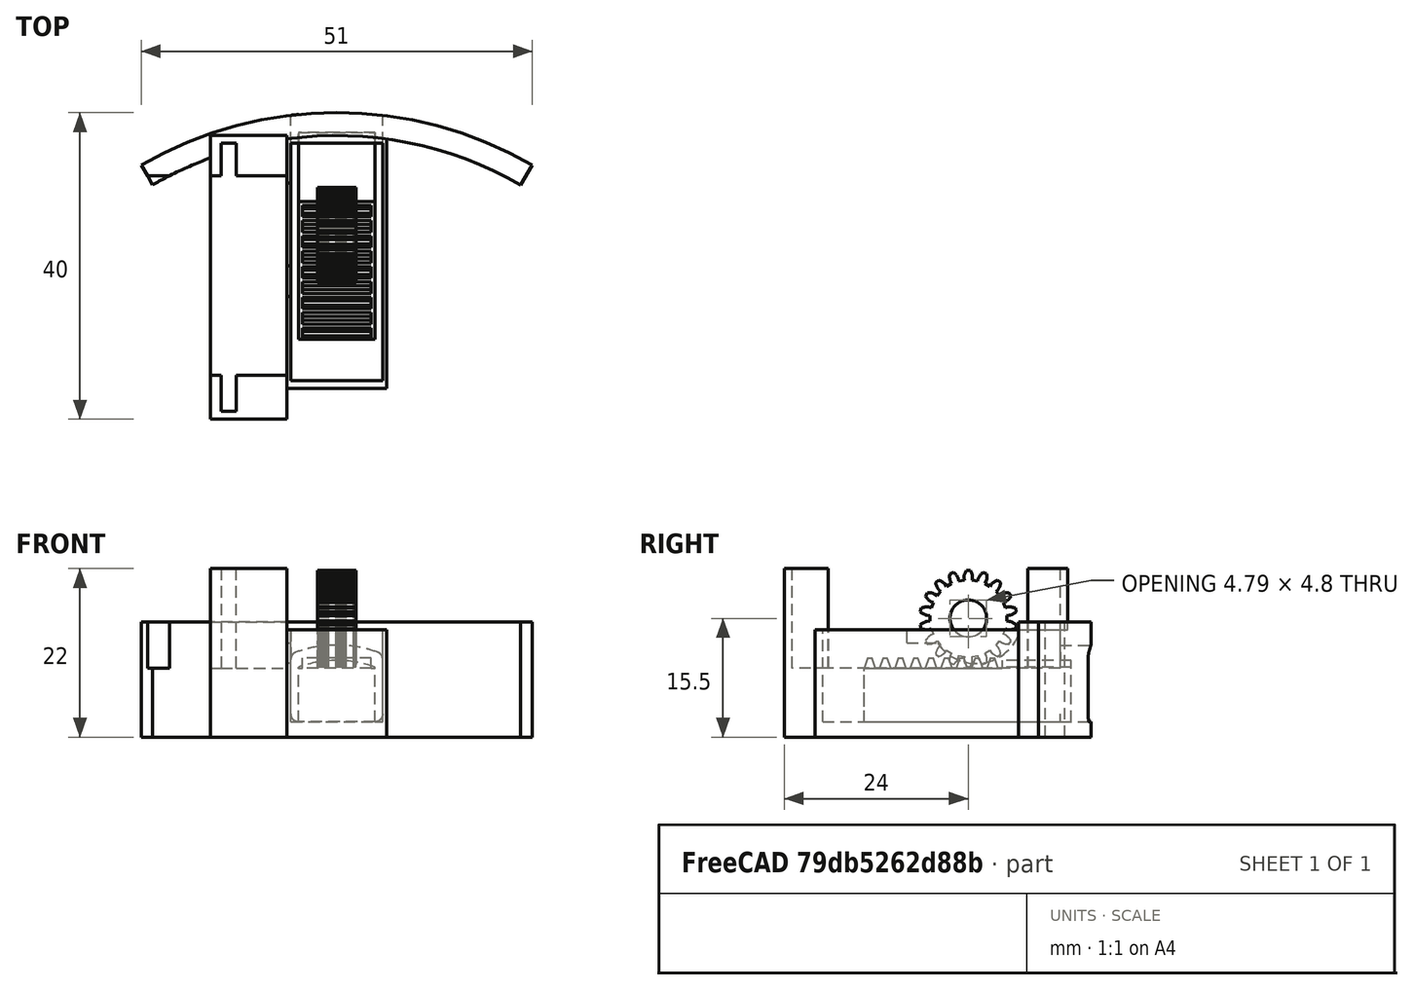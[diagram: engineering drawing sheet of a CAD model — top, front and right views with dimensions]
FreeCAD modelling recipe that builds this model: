
FCSTD DOCUMENT  (FreeCAD 0.16R4924 (Git))
Label: interior_servo_bay_v4p13
License: All rights reserved
LicenseURL: http://en.wikipedia.org/wiki/All_rights_reserved
objects: Part::Feature×11, Part::Box×9, Part::Cut×6, Part::MultiFuse×6, Part::Cylinder×4, Part::Extrusion×3, Part::Thickness×1, Mesh::Feature×1, Part::Fuse×1, Part::FeaturePython×1, Part::Prism×1, Part::MultiCommon×1
note: 44 computed .brp shape members not serialized (recipe doc carries the construction recipe); baked Part::Feature solids carry a one-line shape summary decoded from their .brp

FEATURE [Part::Cylinder] Cylinder  label="bottle_wall"
  Angle = 60
  Height = 15
  Placement = pos=(8.5,-7,0) rot=(0,0,1;1.0472rad)
  Radius = 51
FEATURE [Part::Cylinder] Cylinder001  label="bottle_wall001"
  Angle = 60
  Height = 15
  Placement = pos=(8.5,-7,0) rot=(0,0,1;1.0472rad)
  Radius = 48
FEATURE [Part::Cut] Cut  label="bottle_wall_composite"
  Base = -> Cylinder
  Placement = pos=(0,-2,0) rot=(0,0,1;0rad)
  Tool = -> Cylinder001
FEATURE [Part::Feature] Common_cs  label="pin_cs"
  Placement = pos=(3.5,35,2) rot=(0,0,1;0rad)
  shape: bbox 10 x 2e-07 x 8 mm, 0 faces, 0 solids (baked)
FEATURE [Part::Extrusion] Extrude
  Base = -> Common_cs
  Dir = (0,5,0)
  Solid = true
FEATURE [Part::Thickness] Thickness
  Faces = -> Extrude [Face7]
  Intersection = false
  Join = 0
  Mode = 0
  SelfIntersection = false
  Value = 1
FEATURE [Part::Feature] Common_cs001  label="pin_cs001"
  Placement = pos=(3.5,35,2) rot=(0,0,1;0rad)
  shape: bbox 10 x 2e-07 x 8 mm, 0 faces, 0 solids (baked)
FEATURE [Part::Extrusion] Extrude001
  Base = -> Common_cs001
  Dir = (0,5,0)
  Solid = true
FEATURE [Part::MultiFuse] Fusion  label="bolt_bottle_side_opening"
  Placement = pos=(0,-7,1) rot=(0,0,1;0rad)
  Shapes = -> [Thickness,Extrude,Extrude001]
FEATURE [Part::Box] Box  label="pullBay"
  Height = 15
  Length = 12
  Placement = pos=(2.5,7,2) rot=(0,0,1;0rad)
  Width = 31
FEATURE [Part::Box] Box001  label="Case"
  Height = 14
  Length = 13
  Placement = pos=(2,6,0) rot=(0,0,1;0rad)
  Width = 34
FEATURE [Part::Cut] Cut001  label="cut bay from case"
  Base = -> Box001
  Tool = -> Box
FEATURE [Part::MultiFuse] Fusion001  label="wall plus case"
  Shapes = -> [Cut,Cut001]
FEATURE [Part::Cut] Cut002  label="hole cut out of case"
  Base = -> Fusion001
  Tool = -> Fusion
FEATURE [Mesh::Feature] Mesh  label="servo_motor_2"
  Placement = pos=(33.6,-52,22) rot=(0,0,-1;1.5708rad)
FEATURE [Part::Fuse] union  label="pinion"
FEATURE [Part::FeaturePython] RefineLinearExtrude  # WARN: FeaturePython — macro-defined, semantics opaque (R4)
  Base = -> union
FEATURE [Part::Extrusion] LinearExtrude
  Base = -> RefineLinearExtrude
  Dir = (0,0,5)
  Solid = true
FEATURE [Part::Prism] prism
  Circumradius = 2.4
  Height = 7
  Placement = pos=(0,0,-1) rot=(0,0,1;0rad)
  Polygon = 50
FEATURE [Part::Cut] difference  label="pinion_final"
  Base = -> LinearExtrude
  Placement = pos=(6,26,15.5) rot=(0,1,0;1.5708rad)
  Tool = -> prism
FEATURE [Part::Cylinder] Cylinder002  label="rounded_top"
  Angle = 360
  Height = 40
  Placement = pos=(5,35,-7) rot=(1,0,0;1.5708rad)
  Radius = 15
FEATURE [Part::Box] Box005  label="pin"
  Height = 8
  Length = 10
  Width = 27
FEATURE [Part::MultiCommon] Common  label="rounded pin"
  Shapes = -> [Cylinder002,Box005]
FEATURE [Part::Box] Box006  label="flat_top"
  Height = 10
  Length = 10
  Placement = pos=(0,0,7) rot=(0,0,1;0rad)
  Width = 18
FEATURE [Part::Cut] Cut005
  Base = -> Common
  Placement = pos=(0,11,0) rot=(0,0,1;0rad)
  Tool = -> Box006
FEATURE [Part::Box] cube
  Height = 5
  Length = 18
  Placement = pos=(-12,-4.5,-2.5) rot=(0,0,1;0rad)
  Width = 9
FEATURE [Part::Feature] polyhedron
  Placement = pos=(-11.2451,0,2.5) rot=(0,0,1;0rad)
  shape: bbox 1.51 x 9 x 1.337 mm, 6 faces (baked)
FEATURE [Part::Feature] polyhedron001
  Placement = pos=(-9.24512,0,2.5) rot=(0,0,1;0rad)
  shape: bbox 1.51 x 9 x 1.337 mm, 6 faces (baked)
FEATURE [Part::Feature] polyhedron002
  Placement = pos=(-7.24512,0,2.5) rot=(0,0,1;0rad)
  shape: bbox 1.51 x 9 x 1.337 mm, 6 faces (baked)
FEATURE [Part::Feature] polyhedron003
  Placement = pos=(-5.24512,0,2.5) rot=(0,0,1;0rad)
  shape: bbox 1.51 x 9 x 1.337 mm, 6 faces (baked)
FEATURE [Part::Feature] polyhedron004
  Placement = pos=(-3.24512,0,2.5) rot=(0,0,1;0rad)
  shape: bbox 1.51 x 9 x 1.337 mm, 6 faces (baked)
FEATURE [Part::Feature] polyhedron005
  Placement = pos=(-1.24512,0,2.5) rot=(0,0,1;0rad)
  shape: bbox 1.51 x 9 x 1.337 mm, 6 faces (baked)
FEATURE [Part::Feature] polyhedron006
  Placement = pos=(0.754882,0,2.5) rot=(0,0,1;0rad)
  shape: bbox 1.51 x 9 x 1.337 mm, 6 faces (baked)
FEATURE [Part::Feature] polyhedron007
  Placement = pos=(2.75488,0,2.5) rot=(0,0,1;0rad)
  shape: bbox 1.51 x 9 x 1.337 mm, 6 faces (baked)
FEATURE [Part::Feature] polyhedron008
  Placement = pos=(4.75488,0,2.5) rot=(0,0,1;0rad)
  shape: bbox 1.51 x 9 x 1.337 mm, 6 faces (baked)
FEATURE [Part::MultiFuse] Fusion003  label="rack"
  Placement = pos=(5,23,4.5) rot=(0,0,1;1.5708rad)
  Shapes = -> [cube,polyhedron002,polyhedron003,polyhedron004,polyhedron005,polyhedron,polyhedron007,polyhedron001,polyhedron006,polyhedron008]
FEATURE [Part::MultiFuse] Fusion004  label="pin_3p2"
  Placement = pos=(3.5,1.4,2) rot=(0,0,1;0rad)
  Shapes = -> [Fusion003,Cut005]
FEATURE [Part::Box] Box007  label="mount"
  Height = 22
  Length = 10
  Placement = pos=(-8,2,0) rot=(0,0,1;0rad)
  Width = 37
FEATURE [Part::Box] Box008  label="Cube"
  Height = 13
  Length = 35
  Placement = pos=(-42,1.5,-2) rot=(0,0,1;0rad)
  Width = 2
FEATURE [Part::Box] Box009  label="Cube001"
  Height = 13
  Length = 26
  Placement = pos=(-37.75,-13.6,-2) rot=(0,0,1;0rad)
  Width = 23.7
FEATURE [Part::Box] Box010  label="Cube002"
  Height = 7
  Length = 10
  Placement = pos=(-32,3.3,1.3) rot=(0,0,1;0rad)
  Width = 10
FEATURE [Part::Cylinder] Cylinder003
  Angle = 360
  Height = 6
  Placement = pos=(-31,14.3,4.6) rot=(1,0,0;1.5708rad)
  Radius = 6
FEATURE [Part::MultiFuse] Fusion005  label="simple_servo_rev_eng"
  Placement = pos=(-8.1,-4,11) rot=(0,0,1;4.71239rad)
  Shapes = -> [Box008,Box010,Cylinder003,Box009]
FEATURE [Part::MultiFuse] Fusion006
  Shapes = -> [Box007,Cut002]
FEATURE [Part::Cut] Cut006
  Base = -> Fusion006
  Tool = -> Fusion005
